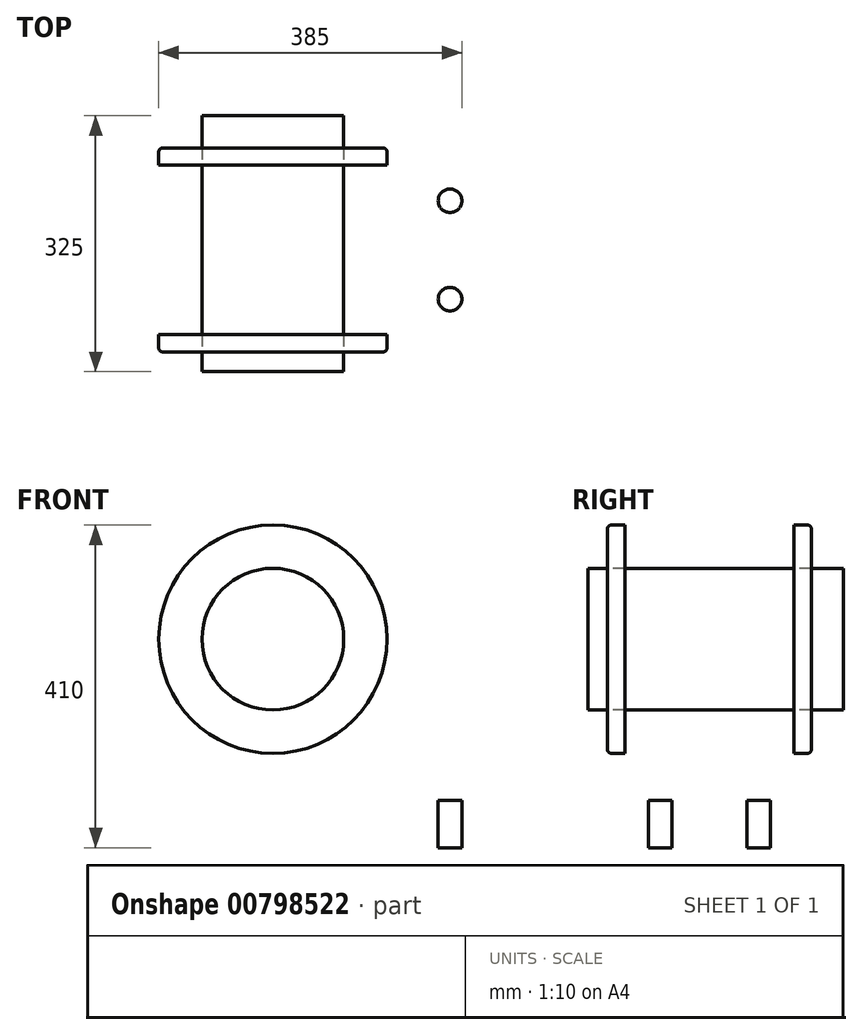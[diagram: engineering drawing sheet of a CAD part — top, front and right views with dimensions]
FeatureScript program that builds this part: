
annotation { "Feature Type Name" : "Feature", "Feature Type Description" : "" }
export const myFeature = defineFeature(function(context is Context, id is Id, definition is map)
    precondition{}
    {
        {
            var Q0;
            Q0=qCreatedBy(makeId("Front.planeOp"),FACE);
            var sketch = newSketch(context, id + "F0", { "sketchPlane" : qUnion([Q0])});
            skCircle(sketch, "E0", {"center": v(0, 0) * mm, "radius": 90 * mm});
            skLineSegment(sketch, "E1.bottom", {"start": v(0, 0) * mm, "end": v(-185, 0) * mm});
            skLineSegment(sketch, "E1.top", {"start": v(0, -265) * mm, "end": v(-270, -265) * mm});
            skLineSegment(sketch, "E1.left", {"start": v(0, 0) * mm, "end": v(0, -265) * mm});
            skLineSegment(sketch, "E1.right", {"start": v(-270, -205) * mm, "end": v(-270, -265) * mm});
            skLineSegment(sketch, "E2.bottom", {"start": v(0, 0) * mm, "end": v(185, 0) * mm});
            skLineSegment(sketch, "E2.top", {"start": v(0, -265) * mm, "end": v(270, -265) * mm});
            skLineSegment(sketch, "E2.right", {"start": v(270, -205) * mm, "end": v(270, -265) * mm});
            skCircle(sketch, "E3", {"center": v(0, 0) * mm, "radius": 145 * mm});
            skLineSegment(sketch, "E4", {"start": v(-185, 0) * mm, "end": v(-185, -205) * mm});
            skLineSegment(sketch, "E5", {"start": v(-185, -205) * mm, "end": v(-270, -205) * mm});
            skLineSegment(sketch, "E6", {"start": v(185, 0) * mm, "end": v(185, -205) * mm});
            skLineSegment(sketch, "E7", {"start": v(185, -205) * mm, "end": v(270, -205) * mm});
            skArc(sketch, "E8", {"start": v(185, 0) * mm, "mid": v(0, 195) * mm, "end": v(-185, 0) * mm});
            skSolve(sketch);
        }
        {
            var Q0;
            {var subQ1=sQuery(id+"F0.wireOp",EDGE,"E2.top");Q0=makeQuery(id+"F0.imprint","IMPRINT",FACE,{"disambiguationData":[TD([[makeQuery(id+"F0.imprint","IMPRINT",EDGE,{"derivedFrom":subQ1}),1.0]])]});}
            var Q1;
            {var subQ0=sQuery(id+"F0.wireOp",EDGE,"E8");Q1=makeQuery(id+"F0.imprint","IMPRINT",FACE,{"disambiguationData":[TD([[makeQuery(id+"F0.imprint","IMPRINT",EDGE,{"derivedFrom":subQ0}),1.0]])]});}
            var Q2;
            {var subQ0=sQuery(id+"F0.wireOp",EDGE,"E1.bottom");var subQ1=sQuery(id+"F0.wireOp",EDGE,"E0");var subQ2=makeQuery(id+"F0.imprint","INTERSECT",VERTEX,{"derivedFrom":[subQ1,subQ0]});Q2=makeQuery(id+"F0.imprint","IMPRINT",FACE,{"disambiguationData":[TD([[makeQuery(id+"F0.imprint","IMPRINT",EDGE,{"disambiguationData":[TD([[subQ2,1.0]])],"derivedFrom":subQ1}),-1.0]])]});}
            var Q3;
            {var subQ1=sQuery(id+"F0.wireOp",EDGE,"E1.top");Q3=makeQuery(id+"F0.imprint","IMPRINT",FACE,{"disambiguationData":[TD([[makeQuery(id+"F0.imprint","IMPRINT",EDGE,{"derivedFrom":subQ1}),-1.0]])]});}
            var Q4;
            {var subQ0=sQuery(id+"F0.wireOp",EDGE,"E1.bottom");var subQ1=sQuery(id+"F0.wireOp",EDGE,"E0");var subQ2=makeQuery(id+"F0.imprint","INTERSECT",VERTEX,{"derivedFrom":[subQ1,subQ0]});Q4=makeQuery(id+"F0.imprint","IMPRINT",FACE,{"disambiguationData":[TD([[makeQuery(id+"F0.imprint","IMPRINT",EDGE,{"disambiguationData":[TD([[subQ2,-1.0]])],"derivedFrom":subQ1}),-1.0]])]});}
            var Q5;
            {var subQ0=sQuery(id+"F0.wireOp",EDGE,"E2.bottom");var subQ1=sQuery(id+"F0.wireOp",EDGE,"E0");var subQ2=makeQuery(id+"F0.imprint","INTERSECT",VERTEX,{"derivedFrom":[subQ1,subQ0]});Q5=makeQuery(id+"F0.imprint","IMPRINT",FACE,{"disambiguationData":[TD([[makeQuery(id+"F0.imprint","IMPRINT",EDGE,{"disambiguationData":[TD([[subQ2,1.0]])],"derivedFrom":subQ1}),-1.0]])]});}
            var Q6;
            {var subQ0=sQuery(id+"F0.wireOp",EDGE,"E2.bottom");var subQ1=sQuery(id+"F0.wireOp",EDGE,"E0");var subQ2=makeQuery(id+"F0.imprint","INTERSECT",VERTEX,{"derivedFrom":[subQ1,subQ0]});Q6=makeQuery(id+"F0.imprint","IMPRINT",FACE,{"disambiguationData":[TD([[makeQuery(id+"F0.imprint","IMPRINT",EDGE,{"disambiguationData":[TD([[subQ2,1.0]])],"derivedFrom":subQ1}),1.0]])]});}
            var Q7;
            {var subQ0=sQuery(id+"F0.wireOp",EDGE,"E1.bottom");var subQ1=sQuery(id+"F0.wireOp",EDGE,"E0");var subQ2=makeQuery(id+"F0.imprint","INTERSECT",VERTEX,{"derivedFrom":[subQ1,subQ0]});Q7=makeQuery(id+"F0.imprint","IMPRINT",FACE,{"disambiguationData":[TD([[makeQuery(id+"F0.imprint","IMPRINT",EDGE,{"disambiguationData":[TD([[subQ2,-1.0]])],"derivedFrom":subQ1}),1.0]])]});}
            var Q8;
            {var subQ0=sQuery(id+"F0.wireOp",EDGE,"E1.bottom");var subQ1=sQuery(id+"F0.wireOp",EDGE,"E0");var subQ2=makeQuery(id+"F0.imprint","INTERSECT",VERTEX,{"derivedFrom":[subQ1,subQ0]});Q8=makeQuery(id+"F0.imprint","IMPRINT",FACE,{"disambiguationData":[TD([[makeQuery(id+"F0.imprint","IMPRINT",EDGE,{"disambiguationData":[TD([[subQ2,1.0]])],"derivedFrom":subQ1}),1.0]])]});}
            extrude(context, id + "F1", {"entities" : qUnion([Q0, Q1, Q2, Q3, Q4, Q5, Q6, Q7, Q8]), "depth" : 215 * mm, "offsetDistance" : 25 * mm});
        }
        {
            var Q0;
            Q0=makeQuery(id+"F1.opExtrude","CAP_FACE",FACE,{"disambiguationData":[OSD([sQuery(id+"F0.wireOp",EDGE,"E1.top"),sQuery(id+"F0.wireOp",EDGE,"E1.right"),sQuery(id+"F0.wireOp",EDGE,"E2.top"),sQuery(id+"F0.wireOp",EDGE,"E2.right"),sQuery(id+"F0.wireOp",EDGE,"E4"),sQuery(id+"F0.wireOp",EDGE,"E5"),sQuery(id+"F0.wireOp",EDGE,"E6"),sQuery(id+"F0.wireOp",EDGE,"E7"),sQuery(id+"F0.wireOp",EDGE,"E8")])],"isStart":true});
            var sketch = newSketch(context, id + "F2", { "sketchPlane" : qUnion([Q0])});
            skCircle(sketch, "E9", {"center": v(0, 0) * mm, "radius": 145 * mm});
            skSolve(sketch);
        }
        {
            var Q0;
            Q0=makeQuery(id+"F2.imprint","IMPRINT",FACE,{"disambiguationData":[TD([[makeQuery(id+"F2.imprint","IMPRINT",EDGE,{"derivedFrom":sQuery(id+"F2.wireOp",EDGE,"E9")}),1.0]])]});
            var Q1;
            Q1=sQuery(id+"F2.wireOp",EDGE,"E9");
            extrude(context, id + "F3", {"entities" : qUnion([Q0]), "surfaceEntities" : qUnion([Q1]), "depth" : 22 * mm, "offsetDistance" : 25 * mm});
        }
        {
            var Q0;
            Q0=makeQuery(id+"F1.opExtrude","CAP_FACE",FACE,{"disambiguationData":[OSD([sQuery(id+"F0.wireOp",EDGE,"E1.top"),sQuery(id+"F0.wireOp",EDGE,"E1.right"),sQuery(id+"F0.wireOp",EDGE,"E2.top"),sQuery(id+"F0.wireOp",EDGE,"E2.right"),sQuery(id+"F0.wireOp",EDGE,"E4"),sQuery(id+"F0.wireOp",EDGE,"E5"),sQuery(id+"F0.wireOp",EDGE,"E6"),sQuery(id+"F0.wireOp",EDGE,"E7"),sQuery(id+"F0.wireOp",EDGE,"E8")])],"isStart":false});
            var sketch = newSketch(context, id + "F4", { "sketchPlane" : qUnion([Q0])});
            skCircle(sketch, "E10", {"center": v(0, 0) * mm, "radius": 145 * mm});
            skSolve(sketch);
        }
        {
            var Q0;
            Q0=makeQuery(id+"F4.imprint","IMPRINT",FACE,{"disambiguationData":[TD([[makeQuery(id+"F4.imprint","IMPRINT",EDGE,{"derivedFrom":sQuery(id+"F4.wireOp",EDGE,"E10")}),1.0]])]});
            extrude(context, id + "F5", {"entities" : qUnion([Q0]), "operationType" : NewBodyOperationType.ADD, "depth" : 22 * mm, "offsetDistance" : 25 * mm});
        }
        {
            var Q0;
            Q0=makeQuery(id+"F1.opExtrude","SWEPT_FACE",FACE,{"disambiguationData":[OSD([sQuery(id+"F0.wireOp",EDGE,"E1.top"),sQuery(id+"F0.wireOp",EDGE,"E2.top")])]});
            var sketch = newSketch(context, id + "F6", { "sketchPlane" : qUnion([Q0])});
            skLineSegment(sketch, "E11", {"start": v(-270, 107.5) * mm, "end": v(270, 107.5) * mm, "construction": true});
            skCircle(sketch, "E12", {"center": v(-225, 45) * mm, "radius": 15 * mm});
            skCircle(sketch, "E13", {"center": v(-225, 170) * mm, "radius": 15 * mm});
            skLineSegment(sketch, "E14", {"start": v(0, 0) * mm, "end": v(0, 215) * mm, "construction": true});
            skCircle(sketch, "E15.MirrorC", {"center": v(225, 45) * mm, "radius": 15 * mm});
            skCircle(sketch, "E16.MirrorC", {"center": v(225, 170) * mm, "radius": 15 * mm});
            skSolve(sketch);
        }
        {
            var Q0;
            Q0=makeQuery(id+"F6.imprint","IMPRINT",FACE,{"disambiguationData":[TD([[makeQuery(id+"F6.imprint","IMPRINT",EDGE,{"derivedFrom":sQuery(id+"F6.wireOp",EDGE,"E13")}),1.0]])]});
            var Q1;
            Q1=makeQuery(id+"F6.imprint","IMPRINT",FACE,{"disambiguationData":[TD([[makeQuery(id+"F6.imprint","IMPRINT",EDGE,{"derivedFrom":sQuery(id+"F6.wireOp",EDGE,"E12")}),1.0]])]});
            var Q2;
            Q2=makeQuery(id+"F6.imprint","IMPRINT",FACE,{"disambiguationData":[TD([[makeQuery(id+"F6.imprint","IMPRINT",EDGE,{"derivedFrom":sQuery(id+"F6.wireOp",EDGE,"E15.MirrorC")}),-1.0]])]});
            var Q3;
            Q3=makeQuery(id+"F6.imprint","IMPRINT",FACE,{"disambiguationData":[TD([[makeQuery(id+"F6.imprint","IMPRINT",EDGE,{"derivedFrom":sQuery(id+"F6.wireOp",EDGE,"E16.MirrorC")}),-1.0]])]});
            extrude(context, id + "F7", {"entities" : qUnion([Q0, Q1, Q2, Q3]), "operationType" : NewBodyOperationType.REMOVE, "endBound" : BoundingType.THROUGH_ALL, "oppositeDirection" : true, "depth" : 25 * mm, "offsetDistance" : 25 * mm});
        }
        {
            var Q0;
            Q0=makeQuery(id+"F1.opExtrude","CAP_EDGE",EDGE,{"disambiguationData":[OSD([sQuery(id+"F0.wireOp",EDGE,"E1.right")])],"isStart":true});
            var Q1;
            Q1=makeQuery(id+"F1.opExtrude","CAP_EDGE",EDGE,{"disambiguationData":[OSD([sQuery(id+"F0.wireOp",EDGE,"E1.right")])],"isStart":false});
            var Q2;
            Q2=makeQuery(id+"F1.opExtrude","SWEPT_EDGE",EDGE,{"disambiguationData":[OSD([sQuery(id+"F0.wireOp",EDGE,"E1.right"),sQuery(id+"F0.wireOp",EDGE,"E5")])]});
            var Q3;
            Q3=makeQuery(id+"F1.opExtrude","CAP_EDGE",EDGE,{"disambiguationData":[OSD([sQuery(id+"F0.wireOp",EDGE,"E4")])],"isStart":true});
            var Q4;
            Q4=makeQuery(id+"F1.opExtrude","CAP_EDGE",EDGE,{"disambiguationData":[OSD([sQuery(id+"F0.wireOp",EDGE,"E5")])],"isStart":true});
            var Q5;
            Q5=makeQuery(id+"F1.opExtrude","CAP_EDGE",EDGE,{"disambiguationData":[OSD([sQuery(id+"F0.wireOp",EDGE,"E4")])],"isStart":false});
            var Q6;
            Q6=makeQuery(id+"F1.opExtrude","CAP_EDGE",EDGE,{"disambiguationData":[OSD([sQuery(id+"F0.wireOp",EDGE,"E5")])],"isStart":false});
            var Q7;
            Q7=makeQuery(id+"F1.opExtrude","CAP_EDGE",EDGE,{"disambiguationData":[OSD([sQuery(id+"F0.wireOp",EDGE,"E8")])],"isStart":true});
            var Q8;
            Q8=makeQuery(id+"F1.opExtrude","CAP_EDGE",EDGE,{"disambiguationData":[OSD([sQuery(id+"F0.wireOp",EDGE,"E8")])],"isStart":false});
            var Q9;
            Q9=makeQuery(id+"F1.opExtrude","CAP_EDGE",EDGE,{"disambiguationData":[OSD([sQuery(id+"F0.wireOp",EDGE,"E6")])],"isStart":true});
            var Q10;
            Q10=makeQuery(id+"F1.opExtrude","CAP_EDGE",EDGE,{"disambiguationData":[OSD([sQuery(id+"F0.wireOp",EDGE,"E7")])],"isStart":true});
            var Q11;
            Q11=makeQuery(id+"F1.opExtrude","CAP_EDGE",EDGE,{"disambiguationData":[OSD([sQuery(id+"F0.wireOp",EDGE,"E2.right")])],"isStart":true});
            var Q12;
            Q12=makeQuery(id+"F1.opExtrude","SWEPT_EDGE",EDGE,{"disambiguationData":[OSD([sQuery(id+"F0.wireOp",EDGE,"E2.right"),sQuery(id+"F0.wireOp",EDGE,"E7")])]});
            var Q13;
            Q13=makeQuery(id+"F1.opExtrude","SWEPT_EDGE",EDGE,{"disambiguationData":[OSD([sQuery(id+"F0.wireOp",EDGE,"E6"),sQuery(id+"F0.wireOp",EDGE,"E7")])]});
            var Q14;
            Q14=makeQuery(id+"F1.opExtrude","CAP_EDGE",EDGE,{"disambiguationData":[OSD([sQuery(id+"F0.wireOp",EDGE,"E6")])],"isStart":false});
            var Q15;
            Q15=makeQuery(id+"F1.opExtrude","CAP_EDGE",EDGE,{"disambiguationData":[OSD([sQuery(id+"F0.wireOp",EDGE,"E7")])],"isStart":false});
            var Q16;
            Q16=makeQuery(id+"F1.opExtrude","CAP_EDGE",EDGE,{"disambiguationData":[OSD([sQuery(id+"F0.wireOp",EDGE,"E2.right")])],"isStart":false});
            var Q17;
            Q17=makeQuery(id+"F1.opExtrude","SWEPT_EDGE",EDGE,{"disambiguationData":[OSD([sQuery(id+"F0.wireOp",EDGE,"E4"),sQuery(id+"F0.wireOp",EDGE,"E5")])]});
            var Q18;
            Q18=makeQuery(id+"F3.opExtrude","CAP_EDGE",EDGE,{"disambiguationData":[OSD([sQuery(id+"F2.wireOp",EDGE,"E9")])],"isStart":false});
            var Q19;
            Q19=makeQuery(id+"F5.opExtrude","CAP_EDGE",EDGE,{"disambiguationData":[OSD([sQuery(id+"F4.wireOp",EDGE,"E10")])],"isStart":false});
            fillet(context, id + "F8", {"entities" : qUnion([Q0, Q1, Q2, Q3, Q4, Q5, Q6, Q7, Q8, Q9, Q10, Q11, Q12, Q13, Q14, Q15, Q16, Q17, Q18, Q19]), "radius" : 5 * mm, "tangentPropagation" : true, "allowEdgeOverflow" : false});
        }
        {
            var Q0;
            Q0=makeQuery(id+"F5.opExtrude","CAP_FACE",FACE,{"disambiguationData":[OSD([sQuery(id+"F4.wireOp",EDGE,"E10")])],"isStart":false});
            var sketch = newSketch(context, id + "F9", { "sketchPlane" : qUnion([Q0])});
            skCircle(sketch, "E17", {"center": v(0, 0) * mm, "radius": 90 * mm});
            skSolve(sketch);
        }
        {
            var Q0;
            Q0=makeQuery(id+"F9.imprint","IMPRINT",FACE,{"disambiguationData":[TD([[makeQuery(id+"F9.imprint","IMPRINT",EDGE,{"derivedFrom":sQuery(id+"F9.wireOp",EDGE,"E17")}),1.0]])]});
            extrude(context, id + "F10", {"entities" : qUnion([Q0]), "oppositeDirection" : true, "depth" : 300 * mm, "offsetDistance" : 25 * mm, "hasSecondDirection" : true, "secondDirectionOppositeDirection" : false, "secondDirectionDepth" : 25 * mm});
        }
    });
